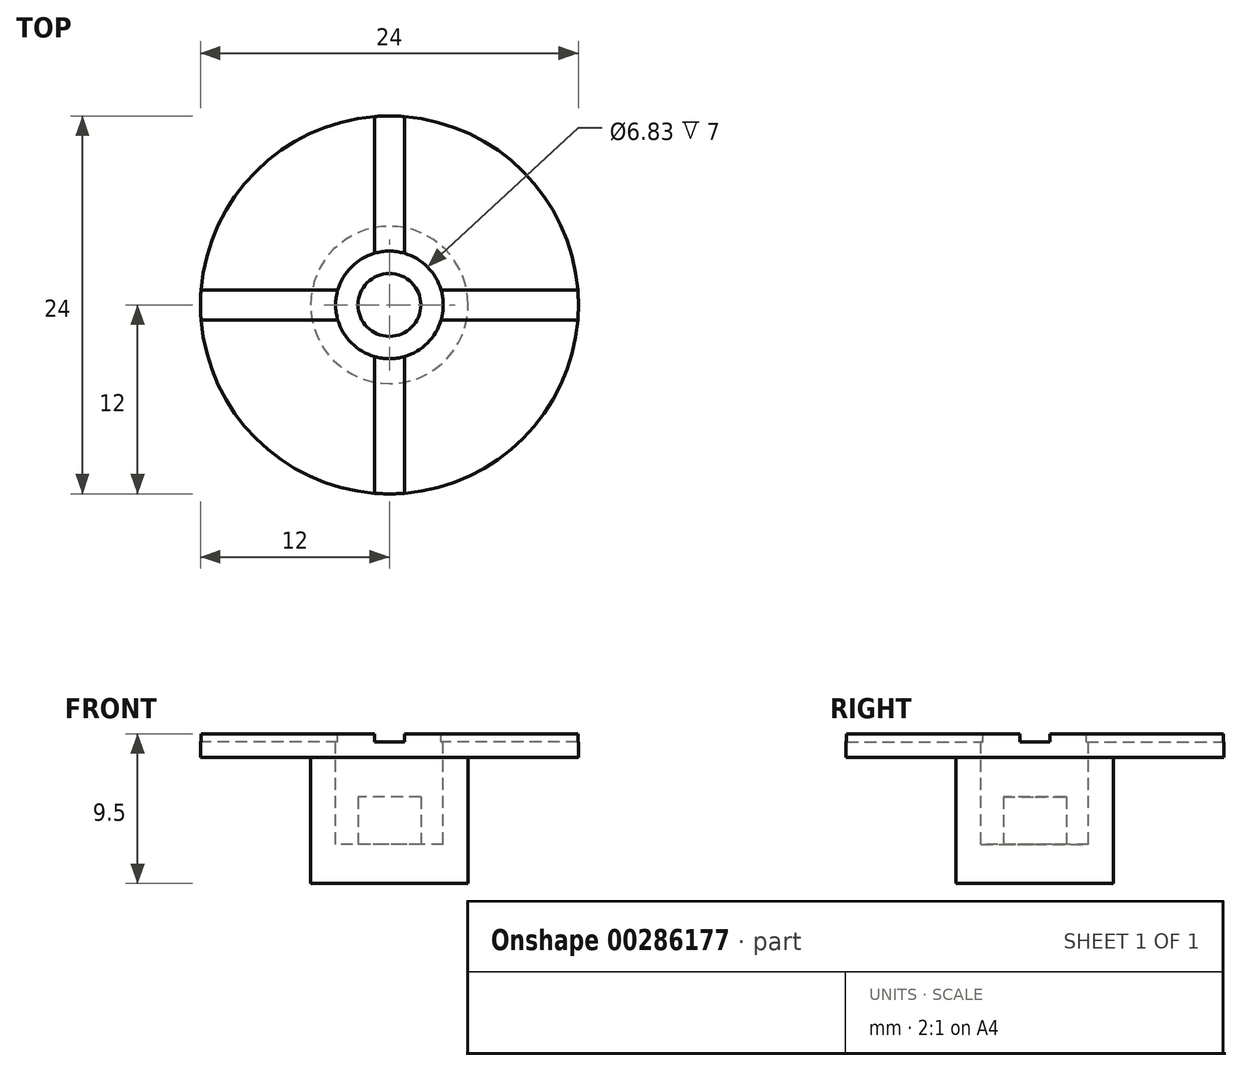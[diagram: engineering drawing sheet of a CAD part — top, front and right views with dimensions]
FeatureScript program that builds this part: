
annotation { "Feature Type Name" : "Feature", "Feature Type Description" : "" }
export const myFeature = defineFeature(function(context is Context, id is Id, definition is map)
    precondition{}
    {
        {
            var Q0;
            Q0=qCreatedBy(makeId("Top.planeOp"),FACE);
            var sketch = newSketch(context, id + "F0", { "sketchPlane" : qUnion([Q0])});
            skCircle(sketch, "E0", {"center": v(0, 0) * mm, "radius": 12 * mm});
            skSolve(sketch);
        }
        {
            var Q0;
            Q0=makeQuery(id+"F0.imprint","IMPRINT",FACE,{"disambiguationData":[TD([[makeQuery(id+"F0.imprint","IMPRINT",EDGE,{"derivedFrom":sQuery(id+"F0.wireOp",EDGE,"E0")}),1.0]])]});
            extrude(context, id + "F1", {"entities" : qUnion([Q0]), "depth" : 1.5 * mm});
        }
        {
            var Q0;
            Q0=makeQuery(id+"F1.opExtrude","CAP_FACE",FACE,{"disambiguationData":[OSD([sQuery(id+"F0.wireOp",EDGE,"E0")])],"isStart":true});
            var sketch = newSketch(context, id + "F2", { "sketchPlane" : qUnion([Q0])});
            skCircle(sketch, "E1", {"center": v(0, 0) * mm, "radius": 5 * mm});
            skSolve(sketch);
        }
        {
            var Q0;
            Q0 = qSketchRegion(id + "F2", true);
            var Q1;
            Q1=makeQuery(id+"F2.imprint","IMPRINT",FACE,{"disambiguationData":[TD([[makeQuery(id+"F2.imprint","IMPRINT",EDGE,{"derivedFrom":sQuery(id+"F2.wireOp",EDGE,"E1")}),1.0]])]});
            extrude(context, id + "F3", {"entities" : qUnion([Q0, Q1]), "operationType" : NewBodyOperationType.ADD, "depth" : 8 * mm});
        }
        {
            var Q0;
            Q0=makeQuery(id+"F1.opExtrude","CAP_FACE",FACE,{"disambiguationData":[OSD([sQuery(id+"F0.wireOp",EDGE,"E0")])],"isStart":false});
            var sketch = newSketch(context, id + "F4", { "sketchPlane" : qUnion([Q0])});
            skCircle(sketch, "E2", {"center": v(0, 0) * mm, "radius": 3.42 * mm});
            skLineSegment(sketch, "E3.bottom", {"start": v(15, -0.95) * mm, "end": v(3.28, -0.95) * mm});
            skLineSegment(sketch, "E3.top", {"start": v(15, 0.95) * mm, "end": v(3.28, 0.95) * mm});
            skLineSegment(sketch, "E3.left", {"start": v(15, -0.95) * mm, "end": v(15, 0.95) * mm});
            skLineSegment(sketch, "E3.right", {"start": v(-15, -0.95) * mm, "end": v(-15, 0.95) * mm});
            skLineSegment(sketch, "E4.bottom", {"start": v(0.95, -15) * mm, "end": v(-0.95, -15) * mm});
            skLineSegment(sketch, "E4.top", {"start": v(0.95, 15) * mm, "end": v(-0.95, 15) * mm});
            skLineSegment(sketch, "E4.left", {"start": v(0.95, -15) * mm, "end": v(0.95, -3.28) * mm});
            skLineSegment(sketch, "E4.right", {"start": v(-0.95, -15) * mm, "end": v(-0.95, -3.28) * mm});
            skLineSegment(sketch, "E5.trimOffspring", {"start": v(0.95, 3.28) * mm, "end": v(0.95, 15) * mm});
            skLineSegment(sketch, "E6.trimOffspring", {"start": v(-0.95, 3.28) * mm, "end": v(-0.95, 15) * mm});
            skLineSegment(sketch, "E7.trimOffspring", {"start": v(-3.28, 0.95) * mm, "end": v(-15, 0.95) * mm});
            skLineSegment(sketch, "E8.trimOffspring", {"start": v(-3.28, -0.95) * mm, "end": v(-15, -0.95) * mm});
            skSolve(sketch);
        }
        {
            var Q0;
            {var subQ0=sQuery(id+"F4.wireOp",EDGE,"E5.trimOffspring");var subQ1=sQuery(id+"F4.wireOp",EDGE,"E2");var subQ2=makeQuery(id+"F4.imprint","INTERSECT",VERTEX,{"derivedFrom":[subQ1,subQ0]});Q0=makeQuery(id+"F4.imprint","IMPRINT",FACE,{"disambiguationData":[TD([[makeQuery(id+"F4.imprint","IMPRINT",EDGE,{"disambiguationData":[TD([[subQ2,-1.0]])],"derivedFrom":subQ1}),-1.0]])]});}
            var Q1;
            {var subQ0=sQuery(id+"F4.wireOp",EDGE,"E7.trimOffspring");var subQ1=sQuery(id+"F4.wireOp",EDGE,"E2");var subQ2=makeQuery(id+"F4.imprint","INTERSECT",VERTEX,{"derivedFrom":[subQ1,subQ0]});Q1=makeQuery(id+"F4.imprint","IMPRINT",FACE,{"disambiguationData":[TD([[makeQuery(id+"F4.imprint","IMPRINT",EDGE,{"disambiguationData":[TD([[subQ2,-1.0]])],"derivedFrom":subQ1}),-1.0]])]});}
            var Q2;
            {var subQ0=sQuery(id+"F4.wireOp",EDGE,"E4.left");var subQ1=sQuery(id+"F4.wireOp",EDGE,"E2");var subQ2=makeQuery(id+"F4.imprint","INTERSECT",VERTEX,{"derivedFrom":[subQ1,subQ0]});Q2=makeQuery(id+"F4.imprint","IMPRINT",FACE,{"disambiguationData":[TD([[makeQuery(id+"F4.imprint","IMPRINT",EDGE,{"disambiguationData":[TD([[subQ2,1.0]])],"derivedFrom":subQ1}),-1.0]])]});}
            var Q3;
            {var subQ0=sQuery(id+"F4.wireOp",EDGE,"E3.bottom");var subQ1=sQuery(id+"F4.wireOp",EDGE,"E2");var subQ2=makeQuery(id+"F4.imprint","INTERSECT",VERTEX,{"derivedFrom":[subQ1,subQ0]});Q3=makeQuery(id+"F4.imprint","IMPRINT",FACE,{"disambiguationData":[TD([[makeQuery(id+"F4.imprint","IMPRINT",EDGE,{"disambiguationData":[TD([[subQ2,-1.0]])],"derivedFrom":subQ1}),-1.0]])]});}
            extrude(context, id + "F5", {"entities" : qUnion([Q0, Q1, Q2, Q3]), "operationType" : NewBodyOperationType.REMOVE, "oppositeDirection" : true, "depth" : .5 * mm});
        }
        {
            var Q0;
            {var subQ0=sQuery(id+"F4.wireOp",EDGE,"E2");var subQ5=makeQuery(id+"F4.imprint","INTERSECT",VERTEX,{"derivedFrom":[subQ0,sQuery(id+"F4.wireOp",EDGE,"E3.top")]});Q0=makeQuery(id+"F4.imprint","IMPRINT",FACE,{"disambiguationData":[TD([[makeQuery(id+"F4.imprint","IMPRINT",EDGE,{"disambiguationData":[TD([[subQ5,-1.0]])],"derivedFrom":subQ0}),1.0]])]});}
            extrude(context, id + "F6", {"entities" : qUnion([Q0]), "operationType" : NewBodyOperationType.REMOVE, "oppositeDirection" : true, "depth" : 7 * mm});
        }
        {
            var Q0;
            Q0=makeQuery(id+"F6.boolean.opBoolean","COPY",FACE,{"derivedFrom":makeQuery(id+"F6.opExtrude","CAP_FACE",FACE,{"disambiguationData":[OSD([sQuery(id+"F4.wireOp",EDGE,"E2")])],"isStart":false})});
            var sketch = newSketch(context, id + "F7", { "sketchPlane" : qUnion([Q0])});
            skCircle(sketch, "E9", {"center": v(0, 0) * mm, "radius": 2 * mm});
            skSolve(sketch);
        }
        {
            var Q0;
            Q0=makeQuery(id+"F7.imprint","IMPRINT",FACE,{"disambiguationData":[TD([[makeQuery(id+"F7.imprint","IMPRINT",EDGE,{"derivedFrom":sQuery(id+"F7.wireOp",EDGE,"E9")}),1.0]])]});
            extrude(context, id + "F8", {"entities" : qUnion([Q0]), "operationType" : NewBodyOperationType.ADD, "depth" : 3 * mm});
        }
    });
